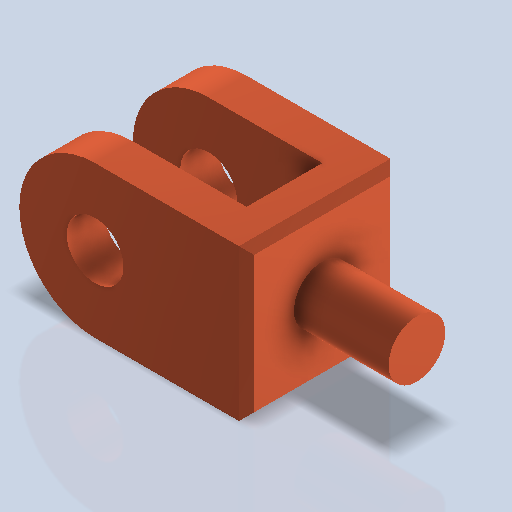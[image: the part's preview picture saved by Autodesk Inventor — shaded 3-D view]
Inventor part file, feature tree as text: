
AUTODESK INVENTOR PART (.ipt)
format: ipt  version: 2024.2 (Build 282272000, 272)  size: 269,312 bytes
history: native  units: mm
features: sketch x4, extrude x3, hole x1, chamfer x1
ambient origin geometry x8: Origin, YZ Plane, XZ Plane, XY Plane, X Axis, Y Axis, Z Axis, Center Point
bodies: Volumenkörper1 (feature_tree)
feature tree (9):
  extrude  "Extrusion1"  Depth=40.0mm
  hole  "Bohrung1"  [1 undecoded]
  extrude  "Extrusion2"  Depth=10.0mm
  chamfer  "Fasen1"  Distance=40.0mm
  extrude  "Extrusion3"  Depth=25.0mm TaperAngle=45.0deg
  sketch  "Skizze1"  dims[d0=40.0mm d2=40.0mm]
  sketch  "Skizze2"  dims[d3=20.0mm d4=40.0mm d5=0.0mm]
  sketch  "Skizze3"  dims[d6=15.0mm d7=6.0mm d8=4.0mm d9=2.0mm d10=90.0deg d11=8.0mm d12=0.0mm d13=10.0mm]
  sketch  "Skizze4"  dims[d14=20.0mm d15=40.0mm d16=0.0mm d17=2.0mm d18=2.0mm d19=45.0deg d20=15.0mm d21=25.0mm d22=0.0mm]
note: 1 required parameter value undecoded (feature->parameter linkage not recoverable at this tier; creation-order binding heuristic only, values carry confidence <= 0.55)
